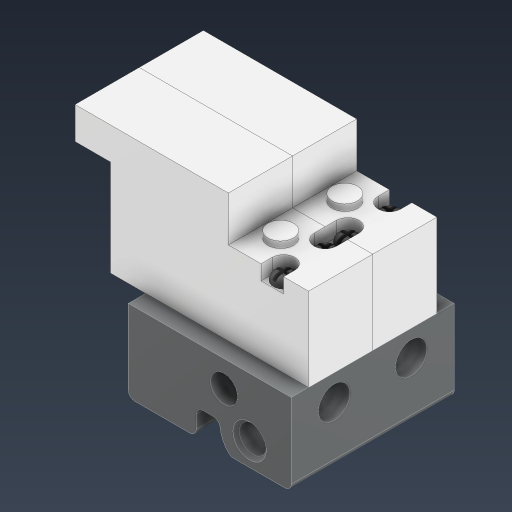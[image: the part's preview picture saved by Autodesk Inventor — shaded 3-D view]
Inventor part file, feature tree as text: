
AUTODESK INVENTOR PART (.ipt)
format: ipt  version: 2024.3 (Build 283343000, 343)  size: 312,832 bytes
history: native  units: in
note: dims shown in document units (in); Inventor stores cm internally (conversion verified against a paired STEP export)
features: fillet x2, other x1
ambient origin geometry x8: Origin, YZ Plane, XZ Plane, XY Plane, X Axis, Y Axis, Z Axis, Center Point
bodies: Solid1 (feature_tree), Solid2 (feature_tree)
feature tree (3):
  other  "Manifold Assembly1"
  fillet  "Fillet3"  [1 undecoded]
  fillet  "Fillet2"  [1 undecoded]
note: 2 required parameter values undecoded (feature->parameter linkage not recoverable at this tier; creation-order binding heuristic only, values carry confidence <= 0.55)
